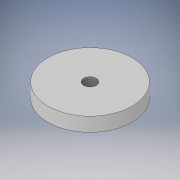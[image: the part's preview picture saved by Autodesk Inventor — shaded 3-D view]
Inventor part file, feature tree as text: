
AUTODESK INVENTOR PART (.ipt)
format: ipt  version: 2019 (Build 230136000, 136)  size: 99,840 bytes
history: native  units: mm
features: sketch x3, extrude x1, hole x1
ambient origin geometry x8: Origin, YZ Plane, XZ Plane, XY Plane, X Axis, Y Axis, Z Axis, Center Point
bodies: Solid1 (feature_tree)
feature tree (5):
  sketch  "Sketch1"  dims[d0=120.0mm d1=20.0mm d2=0.0mm]
  extrude  "Extrusion1"  Depth=20.0mm TaperAngle=0.0deg
  hole  "Hole1"  [1 undecoded]
  sketch  "Sketch2"  dims[d3=17.894mm d4=41.275mm d5=4.0mm d6=2.0mm d7=90.0deg d8=53.975mm d9=20.594885mm d10=0.75mm]
  sketch  "Sketch3"  dims[d11=20.594885mm d12=0.0625mm d13=0.75mm d14=0.375mm]
note: 1 required parameter value undecoded (feature->parameter linkage not recoverable at this tier; creation-order binding heuristic only, values carry confidence <= 0.55)
